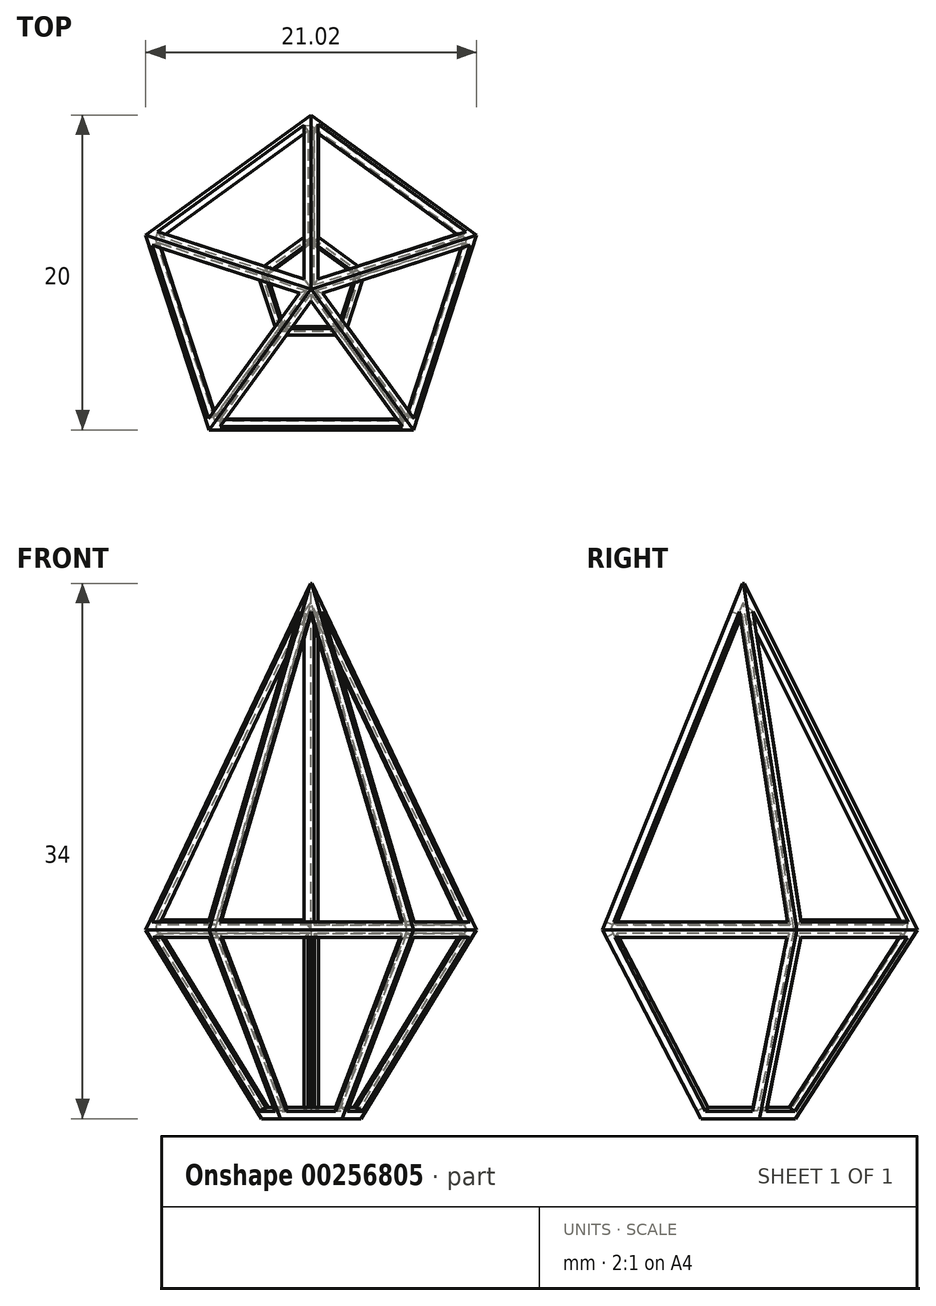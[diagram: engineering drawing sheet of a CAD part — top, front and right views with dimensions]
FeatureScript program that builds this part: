
annotation { "Feature Type Name" : "Feature", "Feature Type Description" : "" }
export const myFeature = defineFeature(function(context is Context, id is Id, definition is map)
    precondition{}
    {
        {
            var Q0;
            Q0=qCreatedBy(makeId("Top.planeOp"),FACE);
            var sketch = newSketch(context, id + "F0", { "sketchPlane" : qUnion([Q0])});
            skCircle(sketch, "E0.cCircle", {"center": v(0, 0) * mm, "radius": 8.94 * mm, "construction": true});
            skLineSegment(sketch, "E0.0", {"start": v(6.5, -8.94) * mm, "end": v(-6.5, -8.94) * mm});
            skLineSegment(sketch, "E0.1", {"start": v(-6.5, -8.94) * mm, "end": v(-10.51, 3.42) * mm});
            skLineSegment(sketch, "E0.2", {"start": v(-10.51, 3.42) * mm, "end": v(0, 11.06) * mm});
            skLineSegment(sketch, "E0.3", {"start": v(0, 11.06) * mm, "end": v(10.51, 3.42) * mm});
            skLineSegment(sketch, "E0.4", {"start": v(10.51, 3.42) * mm, "end": v(6.5, -8.94) * mm});
            skPoint(sketch, "E0.0.midPoint", {"position": v(0, -8.94) * mm});
            skSolve(sketch);
        }
        {
            var Q0;
            Q0=qCreatedBy(makeId("Top.planeOp"),FACE);
            cPlane(context, id + "F1", {"entities" : qUnion([Q0]), "cplaneType" : CPlaneType.OFFSET, "offset" : 22 * mm, "width" : 152.4 * mm, "height" : 152.4 * mm});
        }
        {
            var Q0;
            Q0=qCreatedBy(id+"F1.planeOp",FACE);
            var sketch = newSketch(context, id + "F2", { "sketchPlane" : qUnion([Q0])});
            skCircle(sketch, "E1.cCircle", {"center": v(0, 0) * mm, "radius": 0.04 * mm, "construction": true});
            skLineSegment(sketch, "E1.0", {"start": v(0.03, -0.04) * mm, "end": v(-0.03, -0.04) * mm});
            skLineSegment(sketch, "E1.1", {"start": v(-0.03, -0.04) * mm, "end": v(-0.05, 0.02) * mm});
            skLineSegment(sketch, "E1.2", {"start": v(-0.05, 0.02) * mm, "end": v(0, 0.06) * mm});
            skLineSegment(sketch, "E1.3", {"start": v(0, 0.06) * mm, "end": v(0.05, 0.02) * mm});
            skLineSegment(sketch, "E1.4", {"start": v(0.05, 0.02) * mm, "end": v(0.03, -0.04) * mm});
            skPoint(sketch, "E1.0.midPoint", {"position": v(0, -0.04) * mm});
            skSolve(sketch);
        }
        {
            var Q0;
            Q0=makeQuery(id+"F0.imprint","IMPRINT",FACE,{"disambiguationData":[TD([[makeQuery(id+"F0.imprint","IMPRINT",EDGE,{"derivedFrom":sQuery(id+"F0.wireOp",EDGE,"E0.0")}),-1.0]])]});
            var Q1;
            Q1=makeQuery(id+"F2.imprint","IMPRINT",FACE,{"disambiguationData":[TD([[makeQuery(id+"F2.imprint","IMPRINT",EDGE,{"derivedFrom":sQuery(id+"F2.wireOp",EDGE,"E1.0")}),-1.0]])]});
            loft(context, id + "F3", {"sheetProfilesArray" : [{ "sheetProfileEntities" : qUnion([Q0]) }, { "sheetProfileEntities" : qUnion([Q1]) }]});
        }
        {
            var Q0;
            Q0=qCreatedBy(makeId("Top.planeOp"),FACE);
            cPlane(context, id + "F4", {"entities" : qUnion([Q0]), "cplaneType" : CPlaneType.OFFSET, "offset" : 12 * mm, "oppositeDirection" : true, "width" : 150 * mm, "height" : 150 * mm});
        }
        {
            var Q0;
            Q0=qCreatedBy(id+"F4.planeOp",FACE);
            var sketch = newSketch(context, id + "F5", { "sketchPlane" : qUnion([Q0])});
            skCircle(sketch, "E2.cCircle", {"center": v(0, 0) * mm, "radius": 2.68 * mm, "construction": true});
            skLineSegment(sketch, "E2.0", {"start": v(1.95, -2.68) * mm, "end": v(-1.95, -2.68) * mm});
            skLineSegment(sketch, "E2.1", {"start": v(-1.95, -2.68) * mm, "end": v(-3.15, 1.02) * mm});
            skLineSegment(sketch, "E2.2", {"start": v(-3.15, 1.02) * mm, "end": v(0, 3.32) * mm});
            skLineSegment(sketch, "E2.3", {"start": v(0, 3.32) * mm, "end": v(3.15, 1.02) * mm});
            skLineSegment(sketch, "E2.4", {"start": v(3.15, 1.02) * mm, "end": v(1.95, -2.68) * mm});
            skPoint(sketch, "E2.0.midPoint", {"position": v(0, -2.68) * mm});
            skSolve(sketch);
        }
        {
            var Q1;
            Q1=makeQuery(id+"F3.opLoft","CAP_FACE",FACE,{"disambiguationData":[OSD([makeQuery(id+"F0.imprint","IMPRINT",FACE,{"disambiguationData":[TD([[makeQuery(id+"F0.imprint","IMPRINT",EDGE,{"derivedFrom":sQuery(id+"F0.wireOp",EDGE,"E0.0")}),-1.0]])]})])],"isStart":true});
            var Q2;
            Q2=makeQuery(id+"F5.imprint","IMPRINT",FACE,{"disambiguationData":[TD([[makeQuery(id+"F5.imprint","IMPRINT",EDGE,{"derivedFrom":sQuery(id+"F5.wireOp",EDGE,"E2.0")}),-1.0]])]});
            loft(context, id + "F6", {"operationType" : NewBodyOperationType.ADD, "sheetProfilesArray" : [{ "sheetProfileEntities" : qUnion([Q1]) }, { "sheetProfileEntities" : qUnion([Q2]) }]});
        }
        {
            var Q0;
            Q0=makeQuery(id+"F3.opLoft","SWEPT_FACE",FACE,{"disambiguationData":[OSD([sQuery(id+"F0.wireOp",EDGE,"E0.1"),sQuery(id+"F0.wireOp",EDGE,"E0.2"),sQuery(id+"F0.wireOp",EDGE,"E0.3"),sQuery(id+"F2.wireOp",EDGE,"E1.1"),sQuery(id+"F2.wireOp",EDGE,"E1.2"),sQuery(id+"F2.wireOp",EDGE,"E1.3")])]});
            shell(context, id + "F7", {"entities" : qUnion([Q0]), "thickness" : .5 * mm});
        }
        {
            var Q0;
            Q0=makeQuery(id+"F3.opLoft","SWEPT_FACE",FACE,{"disambiguationData":[OSD([sQuery(id+"F0.wireOp",EDGE,"E0.0"),sQuery(id+"F0.wireOp",EDGE,"E0.1"),sQuery(id+"F0.wireOp",EDGE,"E0.2"),sQuery(id+"F2.wireOp",EDGE,"E1.0"),sQuery(id+"F2.wireOp",EDGE,"E1.1"),sQuery(id+"F2.wireOp",EDGE,"E1.2")])]});
            var sketch = newSketch(context, id + "F8", { "sketchPlane" : qUnion([Q0])});
            skLineSegment(sketch, "E3", {"start": v(-5.4, -3.5) * mm, "end": v(6.1, -2.1) * mm});
            skLineSegment(sketch, "E4", {"start": v(6.1, -2.1) * mm, "end": v(-2.23, 18.31) * mm});
            skLineSegment(sketch, "E5", {"start": v(-2.23, 18.31) * mm, "end": v(-5.4, -3.5) * mm});
            skSolve(sketch);
        }
        {
            var Q0;
            Q0=makeQuery(id+"F3.opLoft","SWEPT_FACE",FACE,{"disambiguationData":[OSD([sQuery(id+"F0.wireOp",EDGE,"E0.0"),sQuery(id+"F0.wireOp",EDGE,"E0.1"),sQuery(id+"F0.wireOp",EDGE,"E0.4"),sQuery(id+"F2.wireOp",EDGE,"E1.0"),sQuery(id+"F2.wireOp",EDGE,"E1.1"),sQuery(id+"F2.wireOp",EDGE,"E1.4")])]});
            var sketch = newSketch(context, id + "F9", { "sketchPlane" : qUnion([Q0])});
            skLineSegment(sketch, "E6", {"start": v(-5.8, -2.81) * mm, "end": v(5.8, -2.81) * mm});
            skLineSegment(sketch, "E7", {"start": v(5.8, -2.81) * mm, "end": v(0, 18.44) * mm});
            skLineSegment(sketch, "E8", {"start": v(0, 18.44) * mm, "end": v(-5.8, -2.81) * mm});
            skSolve(sketch);
        }
        {
            var Q0;
            Q0=makeQuery(id+"F3.opLoft","SWEPT_FACE",FACE,{"disambiguationData":[OSD([sQuery(id+"F0.wireOp",EDGE,"E0.0"),sQuery(id+"F0.wireOp",EDGE,"E0.3"),sQuery(id+"F0.wireOp",EDGE,"E0.4"),sQuery(id+"F2.wireOp",EDGE,"E1.0"),sQuery(id+"F2.wireOp",EDGE,"E1.3"),sQuery(id+"F2.wireOp",EDGE,"E1.4")])]});
            var sketch = newSketch(context, id + "F10", { "sketchPlane" : qUnion([Q0])});
            skLineSegment(sketch, "E9", {"start": v(-6.09, -2.1) * mm, "end": v(5.4, -3.5) * mm});
            skLineSegment(sketch, "E10", {"start": v(5.4, -3.5) * mm, "end": v(2.23, 18.3) * mm});
            skLineSegment(sketch, "E11", {"start": v(2.23, 18.3) * mm, "end": v(-6.09, -2.1) * mm});
            skSolve(sketch);
        }
        {
            var Q0;
            Q0=makeQuery(id+"F3.opLoft","SWEPT_FACE",FACE,{"disambiguationData":[OSD([sQuery(id+"F0.wireOp",EDGE,"E0.2"),sQuery(id+"F0.wireOp",EDGE,"E0.3"),sQuery(id+"F0.wireOp",EDGE,"E0.4"),sQuery(id+"F2.wireOp",EDGE,"E1.2"),sQuery(id+"F2.wireOp",EDGE,"E1.3"),sQuery(id+"F2.wireOp",EDGE,"E1.4")])]});
            var sketch = newSketch(context, id + "F11", { "sketchPlane" : qUnion([Q0])});
            skLineSegment(sketch, "E12", {"start": v(-6.33, -1.2) * mm, "end": v(4.85, -4.24) * mm});
            skLineSegment(sketch, "E13", {"start": v(4.85, -4.24) * mm, "end": v(4.85, 17.8) * mm});
            skLineSegment(sketch, "E14", {"start": v(4.85, 17.8) * mm, "end": v(-6.33, -1.2) * mm});
            skSolve(sketch);
        }
        {
            var Q0;
            Q0=makeQuery(id+"F11.imprint","IMPRINT",FACE,{"disambiguationData":[TD([[makeQuery(id+"F11.imprint","IMPRINT",EDGE,{"derivedFrom":sQuery(id+"F11.wireOp",EDGE,"E12")}),1.0]])]});
            extrude(context, id + "F12", {"entities" : qUnion([Q0]), "operationType" : NewBodyOperationType.REMOVE, "oppositeDirection" : true, "depth" : 1 * mm});
        }
        {
            var Q0;
            Q0=makeQuery(id+"F10.imprint","IMPRINT",FACE,{"disambiguationData":[TD([[makeQuery(id+"F10.imprint","IMPRINT",EDGE,{"derivedFrom":sQuery(id+"F10.wireOp",EDGE,"E9")}),1.0]])]});
            extrude(context, id + "F13", {"entities" : qUnion([Q0]), "operationType" : NewBodyOperationType.REMOVE, "oppositeDirection" : true, "depth" : 1 * mm});
        }
        {
            var Q0;
            Q0=makeQuery(id+"F8.imprint","IMPRINT",FACE,{"disambiguationData":[TD([[makeQuery(id+"F8.imprint","IMPRINT",EDGE,{"derivedFrom":sQuery(id+"F8.wireOp",EDGE,"E3")}),1.0]])]});
            extrude(context, id + "F14", {"entities" : qUnion([Q0]), "operationType" : NewBodyOperationType.REMOVE, "oppositeDirection" : true, "depth" : 1 * mm});
        }
        {
            var Q0;
            Q0=makeQuery(id+"F9.imprint","IMPRINT",FACE,{"disambiguationData":[TD([[makeQuery(id+"F9.imprint","IMPRINT",EDGE,{"derivedFrom":sQuery(id+"F9.wireOp",EDGE,"E6")}),1.0]])]});
            extrude(context, id + "F15", {"entities" : qUnion([Q0]), "operationType" : NewBodyOperationType.REMOVE, "oppositeDirection" : true, "depth" : 1 * mm});
        }
        {
            var Q0;
            Q0=makeQuery(id+"F6.opLoft","SWEPT_FACE",FACE,{"disambiguationData":[OSD([sQuery(id+"F0.wireOp",EDGE,"E0.2"),sQuery(id+"F0.wireOp",EDGE,"E0.3"),sQuery(id+"F0.wireOp",EDGE,"E0.4"),sQuery(id+"F5.wireOp",EDGE,"E2.2"),sQuery(id+"F5.wireOp",EDGE,"E2.3"),sQuery(id+"F5.wireOp",EDGE,"E2.4")])]});
            var sketch = newSketch(context, id + "F16", { "sketchPlane" : qUnion([Q0])});
            skLineSegment(sketch, "E15", {"start": v(4.3, 5.24) * mm, "end": v(-6.6, 1.58) * mm});
            skLineSegment(sketch, "E16", {"start": v(-6.6, 1.58) * mm, "end": v(1.34, -8.9) * mm});
            skLineSegment(sketch, "E17", {"start": v(1.34, -8.9) * mm, "end": v(4.3, -7.9) * mm});
            skLineSegment(sketch, "E18", {"start": v(4.3, -7.9) * mm, "end": v(4.3, 5.24) * mm});
            skSolve(sketch);
        }
        {
            var Q0;
            Q0=makeQuery(id+"F6.opLoft","SWEPT_FACE",FACE,{"disambiguationData":[OSD([sQuery(id+"F0.wireOp",EDGE,"E0.1"),sQuery(id+"F0.wireOp",EDGE,"E0.2"),sQuery(id+"F0.wireOp",EDGE,"E0.3"),sQuery(id+"F5.wireOp",EDGE,"E2.1"),sQuery(id+"F5.wireOp",EDGE,"E2.2"),sQuery(id+"F5.wireOp",EDGE,"E2.3")])]});
            var sketch = newSketch(context, id + "F17", { "sketchPlane" : qUnion([Q0])});
            skLineSegment(sketch, "E19", {"start": v(6.6, 1.58) * mm, "end": v(-4.3, 5.24) * mm});
            skLineSegment(sketch, "E20", {"start": v(-4.3, 5.24) * mm, "end": v(-4.3, -7.9) * mm});
            skLineSegment(sketch, "E21", {"start": v(-1.34, -8.9) * mm, "end": v(-4.3, -7.9) * mm});
            skLineSegment(sketch, "E22", {"start": v(-1.34, -8.9) * mm, "end": v(6.6, 1.58) * mm});
            skSolve(sketch);
        }
        {
            var Q0;
            Q0=makeQuery(id+"F6.opLoft","SWEPT_FACE",FACE,{"disambiguationData":[OSD([sQuery(id+"F0.wireOp",EDGE,"E0.0"),sQuery(id+"F0.wireOp",EDGE,"E0.1"),sQuery(id+"F0.wireOp",EDGE,"E0.2"),sQuery(id+"F5.wireOp",EDGE,"E2.0"),sQuery(id+"F5.wireOp",EDGE,"E2.1"),sQuery(id+"F5.wireOp",EDGE,"E2.2")])]});
            var sketch = newSketch(context, id + "F18", { "sketchPlane" : qUnion([Q0])});
            skLineSegment(sketch, "E23", {"start": v(6.22, 2.7) * mm, "end": v(-5.15, 4.41) * mm});
            skLineSegment(sketch, "E24", {"start": v(-5.15, 4.41) * mm, "end": v(-2.86, -8.53) * mm});
            skLineSegment(sketch, "E25", {"start": v(0.23, -9) * mm, "end": v(-2.86, -8.53) * mm});
            skLineSegment(sketch, "E26", {"start": v(0.23, -9) * mm, "end": v(6.22, 2.7) * mm});
            skSolve(sketch);
        }
        {
            var Q0;
            Q0=makeQuery(id+"F6.opLoft","SWEPT_FACE",FACE,{"disambiguationData":[OSD([sQuery(id+"F0.wireOp",EDGE,"E0.0"),sQuery(id+"F0.wireOp",EDGE,"E0.1"),sQuery(id+"F0.wireOp",EDGE,"E0.4"),sQuery(id+"F5.wireOp",EDGE,"E2.0"),sQuery(id+"F5.wireOp",EDGE,"E2.1"),sQuery(id+"F5.wireOp",EDGE,"E2.4")])]});
            var sketch = newSketch(context, id + "F19", { "sketchPlane" : qUnion([Q0])});
            skLineSegment(sketch, "E27", {"start": v(5.75, 3.6) * mm, "end": v(-5.75, 3.6) * mm});
            skLineSegment(sketch, "E28", {"start": v(-5.75, 3.6) * mm, "end": v(-1.56, -8.86) * mm});
            skLineSegment(sketch, "E29", {"start": v(-1.56, -8.86) * mm, "end": v(1.56, -8.86) * mm});
            skLineSegment(sketch, "E30", {"start": v(1.56, -8.86) * mm, "end": v(5.75, 3.6) * mm});
            skSolve(sketch);
        }
        {
            var Q0;
            Q0=makeQuery(id+"F6.opLoft","SWEPT_FACE",FACE,{"disambiguationData":[OSD([sQuery(id+"F0.wireOp",EDGE,"E0.0"),sQuery(id+"F0.wireOp",EDGE,"E0.3"),sQuery(id+"F0.wireOp",EDGE,"E0.4"),sQuery(id+"F5.wireOp",EDGE,"E2.0"),sQuery(id+"F5.wireOp",EDGE,"E2.3"),sQuery(id+"F5.wireOp",EDGE,"E2.4")])]});
            var sketch = newSketch(context, id + "F20", { "sketchPlane" : qUnion([Q0])});
            skLineSegment(sketch, "E31", {"start": v(5.15, 4.41) * mm, "end": v(-6.22, 2.7) * mm});
            skLineSegment(sketch, "E32", {"start": v(-6.22, 2.7) * mm, "end": v(-0.23, -9) * mm});
            skLineSegment(sketch, "E33", {"start": v(-0.23, -9) * mm, "end": v(2.86, -8.53) * mm});
            skLineSegment(sketch, "E34", {"start": v(2.86, -8.53) * mm, "end": v(5.15, 4.41) * mm});
            skSolve(sketch);
        }
        {
            var Q0;
            Q0=makeQuery(id+"F20.imprint","IMPRINT",FACE,{"disambiguationData":[TD([[makeQuery(id+"F20.imprint","IMPRINT",EDGE,{"derivedFrom":sQuery(id+"F20.wireOp",EDGE,"E31")}),1.0]])]});
            extrude(context, id + "F21", {"entities" : qUnion([Q0]), "operationType" : NewBodyOperationType.REMOVE, "oppositeDirection" : true, "depth" : 1 * mm});
        }
        {
            var Q0;
            Q0=makeQuery(id+"F16.imprint","IMPRINT",FACE,{"disambiguationData":[TD([[makeQuery(id+"F16.imprint","IMPRINT",EDGE,{"derivedFrom":sQuery(id+"F16.wireOp",EDGE,"E15")}),1.0]])]});
            extrude(context, id + "F22", {"entities" : qUnion([Q0]), "operationType" : NewBodyOperationType.REMOVE, "oppositeDirection" : true, "depth" : 1 * mm});
        }
        {
            var Q0;
            Q0=makeQuery(id+"F19.imprint","IMPRINT",FACE,{"disambiguationData":[TD([[makeQuery(id+"F19.imprint","IMPRINT",EDGE,{"derivedFrom":sQuery(id+"F19.wireOp",EDGE,"E27")}),1.0]])]});
            extrude(context, id + "F23", {"entities" : qUnion([Q0]), "operationType" : NewBodyOperationType.REMOVE, "oppositeDirection" : true, "depth" : 1 * mm});
        }
        {
            var Q0;
            Q0=makeQuery(id+"F18.imprint","IMPRINT",FACE,{"disambiguationData":[TD([[makeQuery(id+"F18.imprint","IMPRINT",EDGE,{"derivedFrom":sQuery(id+"F18.wireOp",EDGE,"E23")}),1.0]])]});
            extrude(context, id + "F24", {"entities" : qUnion([Q0]), "operationType" : NewBodyOperationType.REMOVE, "oppositeDirection" : true, "depth" : 1 * mm});
        }
        {
            var Q0;
            Q0=makeQuery(id+"F17.imprint","IMPRINT",FACE,{"disambiguationData":[TD([[makeQuery(id+"F17.imprint","IMPRINT",EDGE,{"derivedFrom":sQuery(id+"F17.wireOp",EDGE,"E19")}),1.0]])]});
            extrude(context, id + "F25", {"entities" : qUnion([Q0]), "operationType" : NewBodyOperationType.REMOVE, "oppositeDirection" : true, "depth" : 1 * mm});
        }
    });
